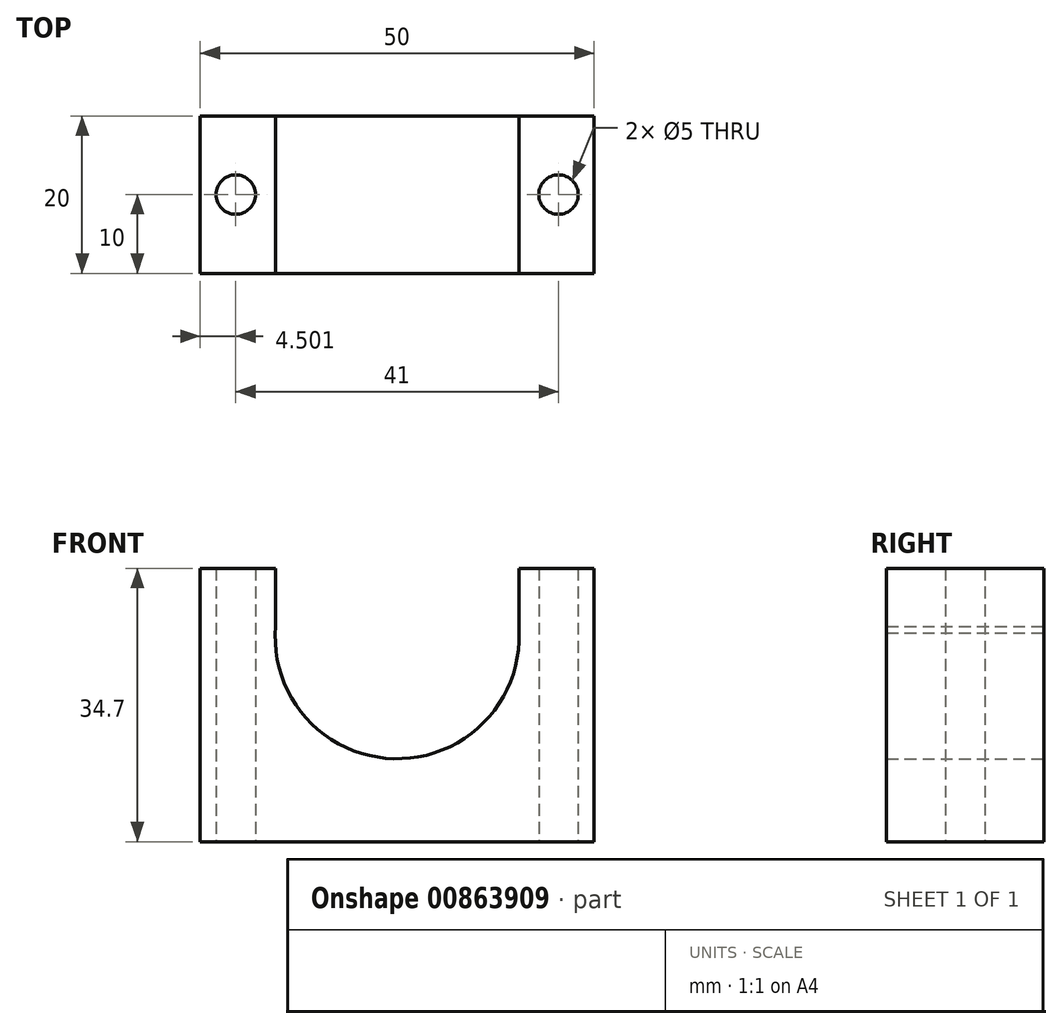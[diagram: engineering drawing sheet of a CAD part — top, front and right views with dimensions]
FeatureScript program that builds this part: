
annotation { "Feature Type Name" : "Feature", "Feature Type Description" : "" }
export const myFeature = defineFeature(function(context is Context, id is Id, definition is map)
    precondition{}
    {
        {
            var Q0;
            Q0=qCreatedBy(makeId("Top.planeOp"),FACE);
            var sketch = newSketch(context, id + "F0", { "sketchPlane" : qUnion([Q0])});
            skLineSegment(sketch, "E0.bottom", {"start": v(-21.73, 0) * mm, "end": v(28.27, 0) * mm});
            skLineSegment(sketch, "E0.top", {"start": v(-21.73, 20) * mm, "end": v(28.27, 20) * mm});
            skLineSegment(sketch, "E0.left", {"start": v(-21.73, 0) * mm, "end": v(-21.73, 20) * mm});
            skLineSegment(sketch, "E0.right", {"start": v(28.27, 0) * mm, "end": v(28.27, 20) * mm});
            skSolve(sketch);
        }
        {
            var Q0;
            Q0 = qSketchRegion(id + "F0", true);
            var Q1;
            Q1=makeQuery(id+"F0.imprint","IMPRINT",FACE,{"disambiguationData":[TD([[makeQuery(id+"F0.imprint","IMPRINT",EDGE,{"derivedFrom":sQuery(id+"F0.wireOp",EDGE,"E0.bottom")}),1.0]])]});
            extrude(context, id + "F1", {"entities" : qUnion([Q0, Q1]), "depth" : 60 * mm, "offsetDistance" : 25 * mm});
        }
        {
            var Q0;
            Q0=makeQuery(id+"F1.opExtrude","SWEPT_FACE",FACE,{"disambiguationData":[OSD([sQuery(id+"F0.wireOp",EDGE,"E0.bottom")])]});
            var sketch = newSketch(context, id + "F2", { "sketchPlane" : qUnion([Q0])});
            skLineSegment(sketch, "E1.bottom", {"start": v(-21.73, 0) * mm, "end": v(28.27, 0) * mm});
            skLineSegment(sketch, "E1.top", {"start": v(-21.73, 34.7) * mm, "end": v(28.27, 34.7) * mm});
            skLineSegment(sketch, "E1.left", {"start": v(-21.73, 0) * mm, "end": v(-21.73, 34.7) * mm});
            skLineSegment(sketch, "E1.right", {"start": v(28.27, 0) * mm, "end": v(28.27, 34.7) * mm});
            skLineSegment(sketch, "E2.bottom", {"start": v(28.27, 0) * mm, "end": v(19.27, 0) * mm});
            skLineSegment(sketch, "E2.top", {"start": v(28.27, 60) * mm, "end": v(19.27, 60) * mm});
            skLineSegment(sketch, "E2.left", {"start": v(28.27, 0) * mm, "end": v(28.27, 60) * mm});
            skLineSegment(sketch, "E2.right", {"start": v(19.27, 0) * mm, "end": v(19.27, 60) * mm});
            skLineSegment(sketch, "E3.bottom", {"start": v(-21.73, 0) * mm, "end": v(-12.73, 0) * mm});
            skLineSegment(sketch, "E3.top", {"start": v(-21.73, 60) * mm, "end": v(-12.73, 60) * mm});
            skLineSegment(sketch, "E3.left", {"start": v(-21.73, 0) * mm, "end": v(-21.73, 60) * mm});
            skLineSegment(sketch, "E3.right", {"start": v(-12.73, 0) * mm, "end": v(-12.73, 60) * mm});
            skSolve(sketch);
        }
        {
            var Q0;
            {var subQ5=sQuery(id+"F2.wireOp",EDGE,"E3.top");Q0=makeQuery(id+"F2.imprint","IMPRINT",FACE,{"disambiguationData":[TD([[makeQuery(id+"F2.imprint","IMPRINT",EDGE,{"derivedFrom":subQ5}),-1.0]])]});}
            var Q1;
            {var subQ5=sQuery(id+"F2.wireOp",EDGE,"E2.top");Q1=makeQuery(id+"F2.imprint","IMPRINT",FACE,{"disambiguationData":[TD([[makeQuery(id+"F2.imprint","IMPRINT",EDGE,{"derivedFrom":subQ5}),-1.0]])]});}
            var Q2;
            {var subQ0=sQuery(id+"F2.wireOp",EDGE,"E3.right");var subQ3=sQuery(id+"F2.wireOp",EDGE,"E1.top");var subQ4=makeQuery(id+"F2.imprint","INTERSECT",VERTEX,{"derivedFrom":[subQ3,subQ0]});Q2=makeQuery(id+"F2.imprint","IMPRINT",FACE,{"disambiguationData":[TD([[makeQuery(id+"F2.imprint","IMPRINT",EDGE,{"disambiguationData":[TD([[subQ4,-1.0]])],"derivedFrom":subQ3}),1.0]])]});}
            extrude(context, id + "F3", {"entities" : qUnion([Q0, Q1, Q2]), "operationType" : NewBodyOperationType.REMOVE, "oppositeDirection" : true, "depth" : 25 * mm, "offsetDistance" : 25 * mm});
        }
        {
            var Q0;
            Q0=makeQuery(id+"F1.opExtrude","CAP_FACE",FACE,{"disambiguationData":[OSD([sQuery(id+"F0.wireOp",EDGE,"E0.bottom"),sQuery(id+"F0.wireOp",EDGE,"E0.top"),sQuery(id+"F0.wireOp",EDGE,"E0.left"),sQuery(id+"F0.wireOp",EDGE,"E0.right")])],"isStart":true});
            var sketch = newSketch(context, id + "F4", { "sketchPlane" : qUnion([Q0])});
            skLineSegment(sketch, "E4.bottom", {"start": v(-21.73, 0) * mm, "end": v(28.27, 0) * mm});
            skLineSegment(sketch, "E4.left", {"start": v(-21.73, 0) * mm, "end": v(-21.73, -10) * mm});
            skLineSegment(sketch, "E4.right", {"start": v(28.27, 0) * mm, "end": v(28.27, -10) * mm});
            skLineSegment(sketch, "E5.bottom", {"start": v(-21.73, 0) * mm, "end": v(-17.23, 0) * mm});
            skLineSegment(sketch, "E5.top", {"start": v(-21.73, -20) * mm, "end": v(-17.23, -20) * mm});
            skLineSegment(sketch, "E5.left", {"start": v(-21.73, 0) * mm, "end": v(-21.73, -20) * mm});
            skLineSegment(sketch, "E6.bottom", {"start": v(28.27, 0) * mm, "end": v(23.77, 0) * mm});
            skLineSegment(sketch, "E6.top", {"start": v(28.27, -20) * mm, "end": v(23.77, -20) * mm});
            skLineSegment(sketch, "E6.left", {"start": v(28.27, 0) * mm, "end": v(28.27, -20) * mm});
            skCircle(sketch, "E7", {"center": v(-17.23, -10) * mm, "radius": 2.5 * mm});
            skCircle(sketch, "E8", {"center": v(23.77, -10) * mm, "radius": 2.5 * mm});
            skSolve(sketch);
        }
        {
            var Q0;
            Q0=makeQuery(id+"F4.imprint","IMPRINT",FACE,{"disambiguationData":[TD([[makeQuery(id+"F4.imprint","IMPRINT",EDGE,{"derivedFrom":sQuery(id+"F4.wireOp",EDGE,"E8")}),1.0]])]});
            var Q1;
            Q1=makeQuery(id+"F4.imprint","IMPRINT",FACE,{"disambiguationData":[TD([[makeQuery(id+"F4.imprint","IMPRINT",EDGE,{"derivedFrom":sQuery(id+"F4.wireOp",EDGE,"E7")}),1.0]])]});
            extrude(context, id + "F5", {"entities" : qUnion([Q0, Q1]), "operationType" : NewBodyOperationType.REMOVE, "oppositeDirection" : true, "depth" : 60 * mm, "offsetDistance" : 25 * mm});
        }
        {
            var Q0;
            Q0=makeQuery(id+"F1.opExtrude","SWEPT_FACE",FACE,{"disambiguationData":[OSD([sQuery(id+"F0.wireOp",EDGE,"E0.top")])]});
            var sketch = newSketch(context, id + "F6", { "sketchPlane" : qUnion([Q0])});
            skLineSegment(sketch, "E9", {"start": v(21.73, 0) * mm, "end": v(-28.27, 0) * mm});
            skCircle(sketch, "E10", {"center": v(-3.27, 26.03) * mm, "radius": 15.5 * mm});
            skSolve(sketch);
        }
        {
            var Q0;
            {var subQ0=sQuery(id+"F6.wireOp",EDGE,"E10");var subQ1=makeQuery(id+"F3.boolean.opBoolean","INTERSECT",EDGE,{"derivedFrom":[makeQuery(id+"F1.opExtrude","SWEPT_FACE",FACE,{"disambiguationData":[OSD([sQuery(id+"F0.wireOp",EDGE,"E0.top")])]}),makeQuery(id+"F3.opExtrude","SWEPT_FACE",FACE,{"disambiguationData":[OSD([sQuery(id+"F2.wireOp",EDGE,"E1.top")])]})]});var subQ2=makeQuery(id+"F6.imprint","INTERSECT",VERTEX,{"disambiguationData":[OD(0.0)],"derivedFrom":[subQ1,subQ0]});Q0=makeQuery(id+"F6.imprint","IMPRINT",FACE,{"disambiguationData":[TD([[makeQuery(id+"F6.imprint","IMPRINT",EDGE,{"disambiguationData":[TD([[subQ2,-1.0]])],"derivedFrom":subQ0}),1.0]])]});}
            var Q1;
            {var subQ0=sQuery(id+"F6.wireOp",EDGE,"E10");var subQ1=makeQuery(id+"F3.boolean.opBoolean","INTERSECT",EDGE,{"derivedFrom":[makeQuery(id+"F1.opExtrude","SWEPT_FACE",FACE,{"disambiguationData":[OSD([sQuery(id+"F0.wireOp",EDGE,"E0.top")])]}),makeQuery(id+"F3.opExtrude","SWEPT_FACE",FACE,{"disambiguationData":[OSD([sQuery(id+"F2.wireOp",EDGE,"E1.top")])]})]});var subQ2=makeQuery(id+"F6.imprint","INTERSECT",VERTEX,{"disambiguationData":[OD(0.0)],"derivedFrom":[subQ1,subQ0]});Q1=makeQuery(id+"F6.imprint","IMPRINT",FACE,{"disambiguationData":[TD([[makeQuery(id+"F6.imprint","IMPRINT",EDGE,{"disambiguationData":[TD([[subQ2,1.0]])],"derivedFrom":subQ0}),1.0]])]});}
            extrude(context, id + "F7", {"entities" : qUnion([Q0, Q1]), "operationType" : NewBodyOperationType.REMOVE, "oppositeDirection" : true, "depth" : 25 * mm, "offsetDistance" : 25 * mm});
        }
        {
            var Q0;
            Q0=makeQuery(id+"F1.opExtrude","SWEPT_FACE",FACE,{"disambiguationData":[OSD([sQuery(id+"F0.wireOp",EDGE,"E0.top")])]});
            var sketch = newSketch(context, id + "F8", { "sketchPlane" : qUnion([Q0])});
            skLineSegment(sketch, "E11", {"start": v(-18.76, 25.55) * mm, "end": v(-18.76, 38.86) * mm});
            skLineSegment(sketch, "E12", {"start": v(12.17, 24.7) * mm, "end": v(12.17, 41.7) * mm});
            skSolve(sketch);
        }
        {
            var Q0;
            {var subQ0=sQuery(id+"F8.wireOp",EDGE,"E11");var subQ3=sQuery(id+"F6.wireOp",EDGE,"E10");var subQ6=makeQuery(id+"F7.boolean.opBoolean","COPY",EDGE,{"derivedFrom":makeQuery(id+"F7.opExtrude","CAP_EDGE",EDGE,{"disambiguationData":[OSD([subQ3])],"isStart":true})});var subQ7=makeQuery(id+"F8.imprint","INTERSECT",VERTEX,{"disambiguationData":[OD(1.0)],"derivedFrom":[subQ6,subQ0]});Q0=makeQuery(id+"F8.imprint","IMPRINT",FACE,{"disambiguationData":[TD([[makeQuery(id+"F8.imprint","IMPRINT",EDGE,{"disambiguationData":[TD([[subQ7,-1.0]])],"derivedFrom":subQ0}),-1.0]])]});}
            var Q1;
            {var subQ0=sQuery(id+"F8.wireOp",EDGE,"E12");var subQ3=sQuery(id+"F6.wireOp",EDGE,"E10");var subQ6=makeQuery(id+"F7.boolean.opBoolean","COPY",EDGE,{"derivedFrom":makeQuery(id+"F7.opExtrude","CAP_EDGE",EDGE,{"disambiguationData":[OSD([subQ3])],"isStart":true})});var subQ7=makeQuery(id+"F8.imprint","INTERSECT",VERTEX,{"disambiguationData":[OD(1.0)],"derivedFrom":[subQ6,subQ0]});Q1=makeQuery(id+"F8.imprint","IMPRINT",FACE,{"disambiguationData":[TD([[makeQuery(id+"F8.imprint","IMPRINT",EDGE,{"disambiguationData":[TD([[subQ7,-1.0]])],"derivedFrom":subQ0}),1.0]])]});}
            extrude(context, id + "F9", {"entities" : qUnion([Q0, Q1]), "operationType" : NewBodyOperationType.REMOVE, "oppositeDirection" : true, "depth" : 25 * mm, "offsetDistance" : 25 * mm});
        }
    });
